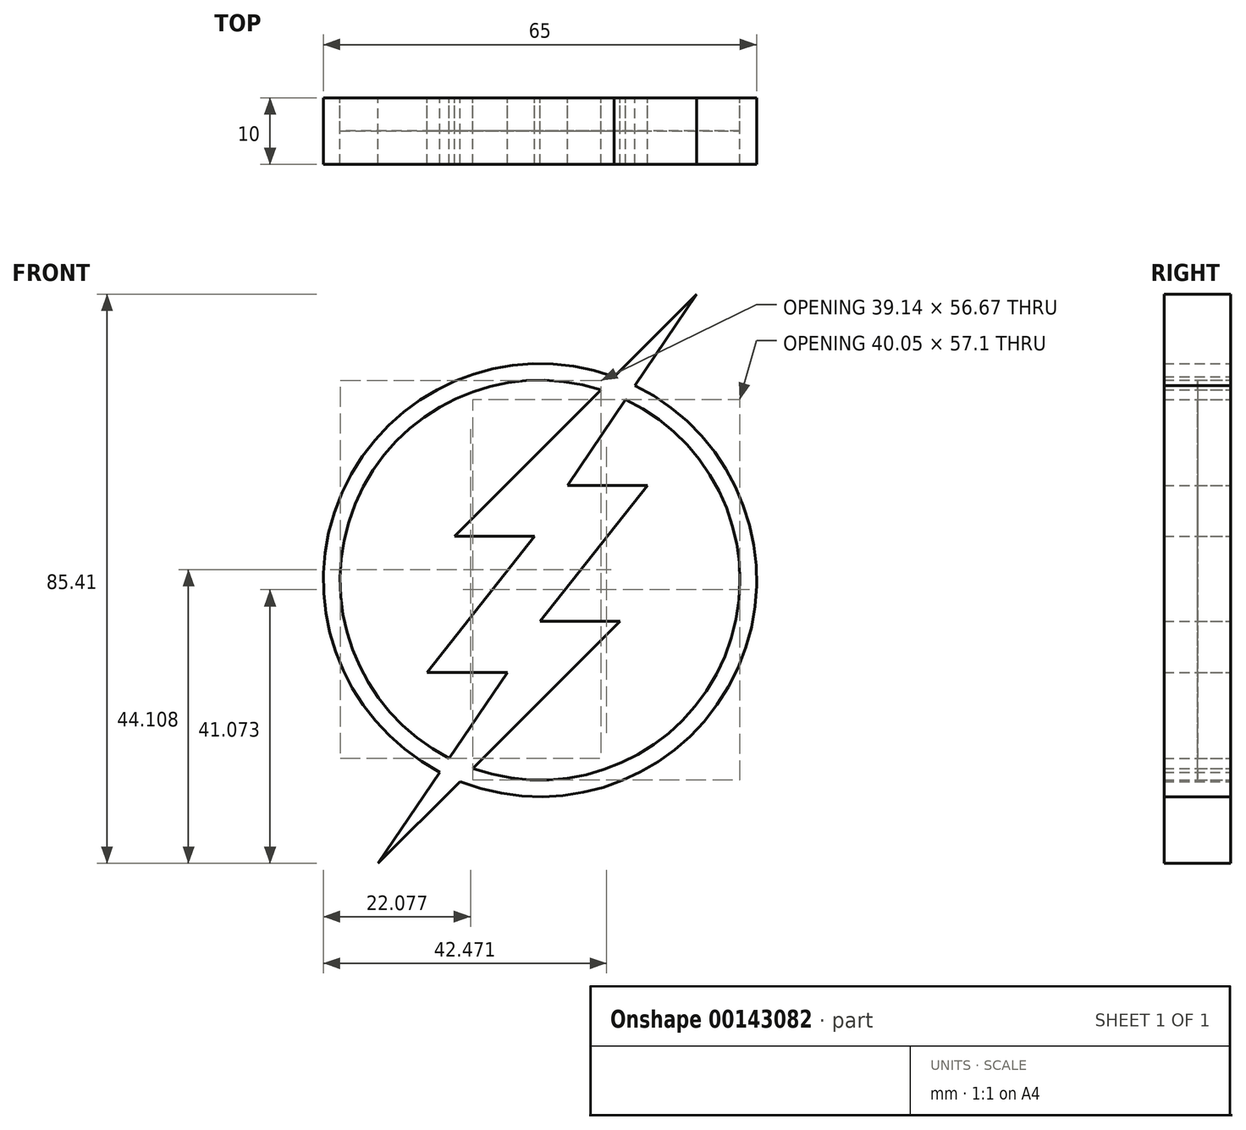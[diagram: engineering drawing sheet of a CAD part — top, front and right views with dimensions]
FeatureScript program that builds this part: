
annotation { "Feature Type Name" : "Feature", "Feature Type Description" : "" }
export const myFeature = defineFeature(function(context is Context, id is Id, definition is map)
    precondition{}
    {
        {
            var Q0;
            Q0=qCreatedBy(makeId("Front.planeOp"),FACE);
            var sketch = newSketch(context, id + "F0", { "sketchPlane" : qUnion([Q0])});
            skArc(sketch, "E0", {"start": v(9.15, 28.57) * mm, "mid": v(-27.74, 11.43) * mm, "end": v(-13.63, -26.73) * mm});
            skArc(sketch, "E1", {"start": v(11.12, 30.54) * mm, "mid": v(-29.74, 13.1) * mm, "end": v(-15.04, -28.81) * mm});
            skPoint(sketch, "E2.endSnap0", {"position": v(-9.96, 2.2) * mm});
            skLineSegment(sketch, "E3", {"start": v(23.48, 42.91) * mm, "end": v(11.12, 30.54) * mm});
            skLineSegment(sketch, "E4", {"start": v(-0.8, 6.6) * mm, "end": v(-16.91, -13.83) * mm});
            skLineSegment(sketch, "E5", {"start": v(-16.91, -13.83) * mm, "end": v(-4.91, -13.83) * mm});
            skPoint(sketch, "E5.endSnap0", {"position": v(-4.91, 4.48) * mm});
            skLineSegment(sketch, "E6", {"start": v(-4.91, -13.83) * mm, "end": v(-13.63, -26.73) * mm});
            skLineSegment(sketch, "E7", {"start": v(-12.8, 6.6) * mm, "end": v(-0.8, 6.6) * mm});
            skLineSegment(sketch, "E8", {"start": v(-24.29, -42.5) * mm, "end": v(-12, -30.2) * mm});
            skLineSegment(sketch, "E9", {"start": v(12, -6.2) * mm, "end": v(0, -6.2) * mm});
            skLineSegment(sketch, "E10", {"start": v(0, -6.2) * mm, "end": v(16.1, 14.24) * mm});
            skLineSegment(sketch, "E11", {"start": v(16.1, 14.24) * mm, "end": v(4.1, 14.24) * mm});
            skLineSegment(sketch, "E12", {"start": v(4.1, 14.24) * mm, "end": v(12.82, 27.12) * mm});
            skLineSegment(sketch, "E13.trimOffspring", {"start": v(9.15, 28.57) * mm, "end": v(-12.8, 6.6) * mm});
            skLineSegment(sketch, "E14.trimOffspring", {"start": v(14.23, 29.22) * mm, "end": v(23.48, 42.91) * mm});
            skLineSegment(sketch, "E15.trimOffspring", {"start": v(-15.04, -28.81) * mm, "end": v(-24.29, -42.5) * mm});
            skArc(sketch, "E16.trimOffspring", {"start": v(-10.06, -28.26) * mm, "mid": v(27.73, -11.45) * mm, "end": v(12.82, 27.12) * mm});
            skLineSegment(sketch, "E17.trimOffspring", {"start": v(-10.06, -28.26) * mm, "end": v(12, -6.2) * mm});
            skArc(sketch, "E18.trimOffspring", {"start": v(-12, -30.2) * mm, "mid": v(29.73, -13.12) * mm, "end": v(14.23, 29.22) * mm});
            skLineSegment(sketch, "E19", {"start": v(9.15, 28.57) * mm, "end": v(11.12, 30.54) * mm});
            skLineSegment(sketch, "E20", {"start": v(14.23, 29.22) * mm, "end": v(12.82, 27.12) * mm});
            skLineSegment(sketch, "E21", {"start": v(-15.04, -28.81) * mm, "end": v(-13.63, -26.73) * mm});
            skLineSegment(sketch, "E22", {"start": v(-10.06, -28.26) * mm, "end": v(-12, -30.2) * mm});
            skSolve(sketch);
        }
        {
            var Q0;
            Q0=makeQuery(id+"F0.imprint","IMPRINT",FACE,{"disambiguationData":[TD([[makeQuery(id+"F0.imprint","IMPRINT",EDGE,{"derivedFrom":sQuery(id+"F0.wireOp",EDGE,"E0")}),1.0]])]});
            var Q1;
            Q1=makeQuery(id+"F0.imprint","IMPRINT",FACE,{"disambiguationData":[TD([[makeQuery(id+"F0.imprint","IMPRINT",EDGE,{"derivedFrom":sQuery(id+"F0.wireOp",EDGE,"E9")}),-1.0]])]});
            extrude(context, id + "F1", {"entities" : qUnion([Q0, Q1]), "depth" : 5 * mm});
        }
        {
            var Q0;
            Q0 = qSketchRegion(id + "F0", true);
            extrude(context, id + "F2", {"entities" : qUnion([Q0]), "depth" : 10 * mm});
        }
    });
